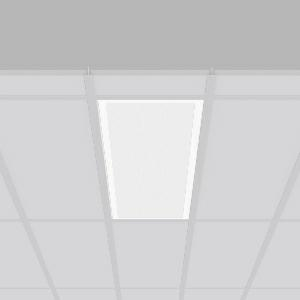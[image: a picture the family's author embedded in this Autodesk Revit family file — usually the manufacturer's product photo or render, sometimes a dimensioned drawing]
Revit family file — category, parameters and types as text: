
# Revit family: sidelite_eco_672374_002_1_04_1de9
name_source: partatom
category: Lighting Fixtures
units: mm (PartAtom-declared; Revit-internal decimal feet)

## family parameters
Cut with Voids When Loaded = No
Host = Face
Light Source = No
Part Type = Normal
Room Calculation Point = No
Round Connector Dimension = Use Diameter
Shared = No

## types (1)
- SIDELITE ECO (1 x LED Modul 840, 3500 lm, 4000)
    Apparent Load = 29 VA
    CIE Flux Codes = 59 87 97 100 100
    Color Rendering = 80
    Color Temperature = 4000
    Default Elevation = 1800 mm
    Description = Series: SIDELITE ECO
Highly economical recessed luminaire with progressive LED technology. For escape route illumination. Frame made of aluminium, powder-coated. Diffuser plastic microprismatic. Lightguide and diffuser made of non-yellowing plastic (PMMA). Lateral light emission (RZB SIDELITE technology) for homogeneous light distribution. External driver. Self-contained system with automatic self-test and feedback to the RZB monitoring system MULTIDIGIT. External driver with simple plug-in locking system. Extended connection cable (1.90 m). 
Colour: white
Length: 1245 mm
Width: 308 mm
Cut-out length: 1220 mm
Cut-out width: 285 mm
Recess height: 160 mm
Luminaire: recess height: 40 mm
Weight: 4.7 kg
Operating mode: maintained power mode
Duration time: 3 h
Lamp: LED
Socket: without socket
Colour temperature: 4000K
Colour rendering index (CRI): 80
System power: 29 W
Rated luminous flux: 3500 lm
Luminous flux, emergency: 510 lm
System power, emergency: -
Control gear: Regulated power supply
Protection class: I
Type of protection: IP 20
    Height = 0 mm  [stored 0 ft]
    Lamp = 1 x LED Modul 840
    Lamp Light Flux = 3500 lm
    Lamp count = 1
    Length = 1245 mm
    Lifetime = 50000 h
    Luminous efficacy = 121 lm/W
    Manufacturer = RZB
    ModVariant = No
    Model = 672374.002.1.04
    Mounting Place = Ceiling
    Mounting Type = Recessed
    Number of Poles = 1
    OnlyDefault = Yes
    Power Factor = 1
    Product Name = SIDELITE ECO
    Product group = Recessed modular luminaires
    ProductGroupID = 406
    Protection Class = Protection class I
    Protection Degree = IP 20
    RLX_Detail_Level = 1
    RLX_Emergency_Light_Flux = 510 lm
    RLX_Emergency_Type = 3
    RLX_Emergency_Type_DB = Yes
    RlxData = <blob elided: 34209 chars, md5=e6ef9845>
    Socket = socket
    Standby Power = 0 W
    System Light Flux = 3500 lm
    System Power = 29 W
    Type Comments = Product without accessories
    Type Image = 312368.002.jpg
    URL = http://relux.com
    VarID = ---
    Voltage = 230 V
    Voltage Range = 220-240 V
    Weight = 0.00 kg
    Width = 308 mm

note: [stored X ft] marks values corroborated as IEEE doubles in the binary element streams (Revit-internal decimal feet)

## geometry (parser evidence)
native form markers: Blend x4, Sweep x12
no freeform markers — native parametric forms only
